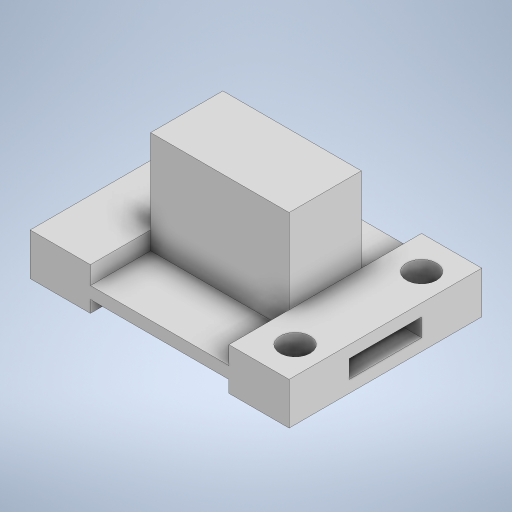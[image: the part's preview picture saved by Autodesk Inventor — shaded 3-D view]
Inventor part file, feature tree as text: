
AUTODESK INVENTOR PART (.ipt)
format: ipt  version: 2023.2 (Build 272271000, 271)  size: 407,040 bytes
history: native  units: mm
features: sketch x6, extrude x1
ambient origin geometry x8: Origin, YZ Plane, XZ Plane, XY Plane, X Axis, Y Axis, Z Axis, Center Point
bodies: Body1 (feature_tree)
feature tree (7):
  sketch  "Sketch1"  dims[d230=31.0mm d231=12.0mm]
  extrude  "Extrusion26"  Depth=12.0mm
  sketch  "Sketch2"  dims[d232=23.0mm]
  sketch  "Sketch3"  dims[d234=4.0mm]
  sketch  "Sketch5"  dims[d235=3.0mm d236=0.0mm]
  sketch  "Sketch7"  dims[d237=19.0mm d238=4.0mm d239=0.0mm d240=0.0mm]
  sketch  "Sketch22"  dims[d241=10.0mm d242=32.0mm d243=10.0mm d244=32.0mm d245=2.0mm d246=0.0mm d247=2.0mm d248=0.0mm d251=3.0mm d252=0.0mm d253=2.0mm d254=0.0mm d255=12.0mm d256=6.0mm d257=6.0mm d258=4.0mm d259=0.0mm d260=5.0mm d261=3.5mm d262=3.0mm d263=0.0mm d266=2.0mm d267=6.0mm d268=6.0mm d269=6.0mm d270=0.0mm d271=5.0mm d272=5.0mm d273=21.0mm d274=5.5mm d275=8.0mm d276=0.0mm d9=0.5mm d10=0.872665mm d11=0.5mm d12=0.872665mm d13=0.5mm d14=0.872665mm d27=0.5mm d28=0.872665mm d29=0.5mm d30=0.872665mm d88=0.5mm d89=0.872665mm d90=0.5mm d91=0.872665mm d116=0.5mm d117=0.872665mm d118=0.5mm d119=0.872665mm d154=0.5mm d155=0.872665mm d156=0.5mm d157=0.872665mm d181=0.5mm d182=0.872665mm d183=0.5mm d184=0.872665mm d221=0.5mm d222=0.872665mm d223=0.5mm d224=0.872665mm]
